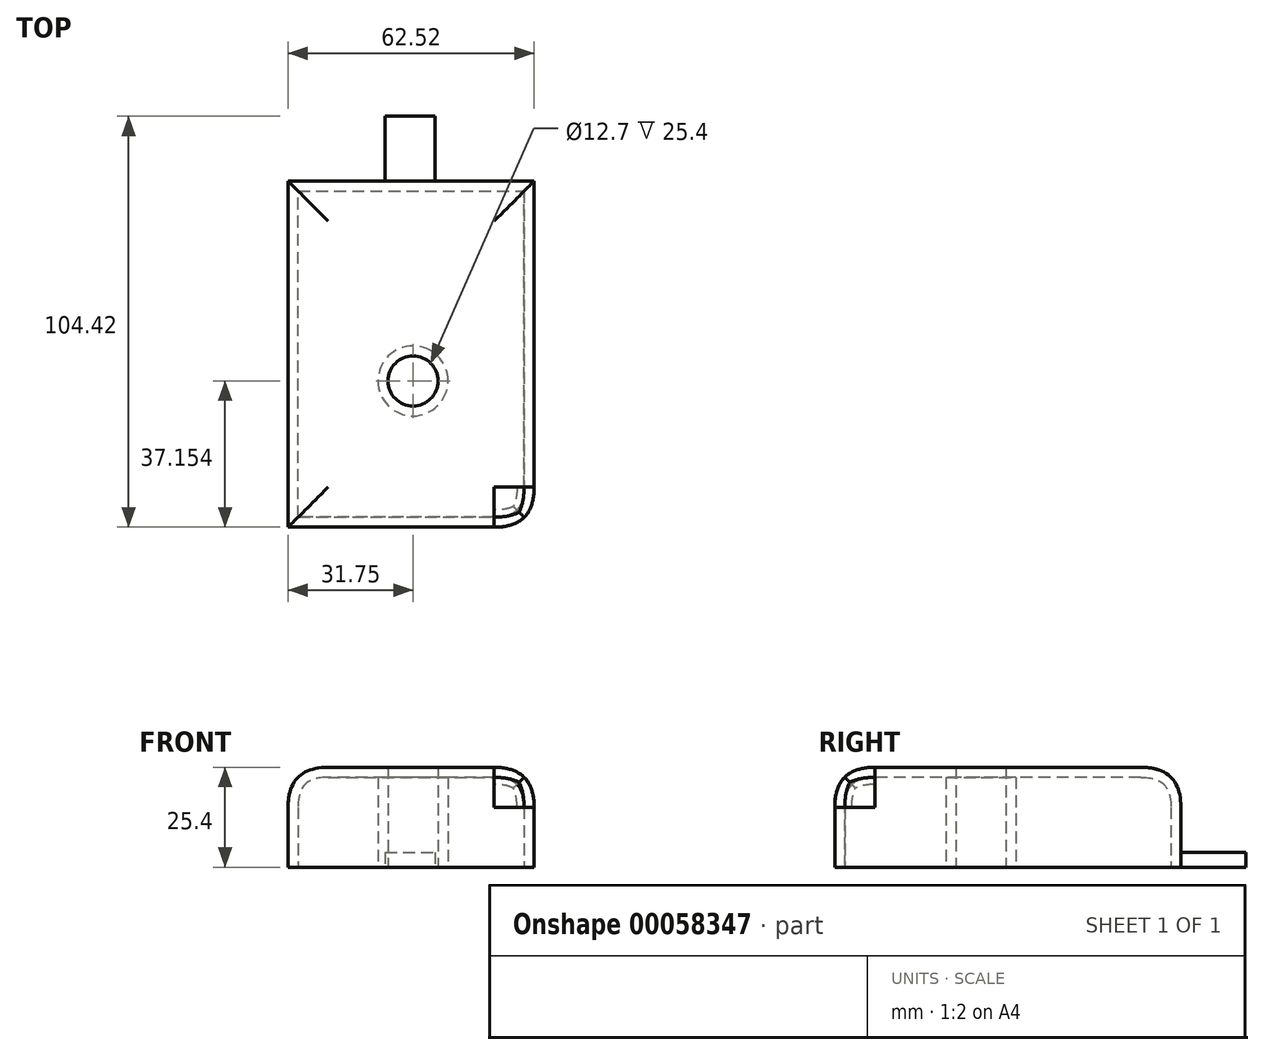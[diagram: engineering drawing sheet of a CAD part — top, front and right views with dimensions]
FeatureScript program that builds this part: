
annotation { "Feature Type Name" : "Feature", "Feature Type Description" : "" }
export const myFeature = defineFeature(function(context is Context, id is Id, definition is map)
    precondition{}
    {
        {
            var Q0;
            Q0=qCreatedBy(makeId("Top.planeOp"),FACE);
            var sketch = newSketch(context, id + "F0", { "sketchPlane" : qUnion([Q0])});
            skLineSegment(sketch, "E0.bottom", {"start": v(0, 0) * mm, "end": v(62.52, 0) * mm});
            skLineSegment(sketch, "E0.top", {"start": v(0, 87.95) * mm, "end": v(62.52, 87.95) * mm});
            skLineSegment(sketch, "E0.left", {"start": v(0, 0) * mm, "end": v(0, 87.95) * mm});
            skLineSegment(sketch, "E0.right", {"start": v(62.52, 0) * mm, "end": v(62.52, 87.95) * mm});
            skSolve(sketch);
        }
        {
            var Q0;
            Q0=makeQuery(id+"F0.imprint","IMPRINT",FACE,{"disambiguationData":[TD([[makeQuery(id+"F0.imprint","IMPRINT",EDGE,{"derivedFrom":sQuery(id+"F0.wireOp",EDGE,"E0.bottom")}),1.0]])]});
            extrude(context, id + "F1", {"entities" : qUnion([Q0]), "depth" : 25.4 * mm});
        }
        {
            var Q0;
            Q0=makeQuery(id+"F1.opExtrude","CAP_FACE",FACE,{"disambiguationData":[OSD([sQuery(id+"F0.wireOp",EDGE,"E0.bottom"),sQuery(id+"F0.wireOp",EDGE,"E0.top"),sQuery(id+"F0.wireOp",EDGE,"E0.left"),sQuery(id+"F0.wireOp",EDGE,"E0.right")])],"isStart":false});
            var sketch = newSketch(context, id + "F2", { "sketchPlane" : qUnion([Q0])});
            skPoint(sketch, "E1", {"position": v(31.75, 37.15) * mm});
            skSolve(sketch);
        }
        {
            var Q0;
            Q0=makeQuery(id+"F1.opExtrude","CAP_EDGE",EDGE,{"disambiguationData":[OSD([sQuery(id+"F0.wireOp",EDGE,"E0.right")])],"isStart":false});
            var Q1;
            Q1=makeQuery(id+"F1.opExtrude","CAP_EDGE",EDGE,{"disambiguationData":[OSD([sQuery(id+"F0.wireOp",EDGE,"E0.bottom")])],"isStart":false});
            var Q2;
            Q2=makeQuery(id+"F1.opExtrude","CAP_EDGE",EDGE,{"disambiguationData":[OSD([sQuery(id+"F0.wireOp",EDGE,"E0.left")])],"isStart":false});
            var Q3;
            Q3=makeQuery(id+"F1.opExtrude","CAP_EDGE",EDGE,{"disambiguationData":[OSD([sQuery(id+"F0.wireOp",EDGE,"E0.top")])],"isStart":false});
            var Q4;
            Q4=makeQuery(id+"F1.opExtrude","SWEPT_EDGE",EDGE,{"disambiguationData":[OSD([sQuery(id+"F0.wireOp",EDGE,"E0.bottom"),sQuery(id+"F0.wireOp",EDGE,"E0.right")])]});
            fillet(context, id + "F3", {"entities" : qUnion([Q0, Q1, Q2, Q3, Q4]), "radius" : 10.16 * mm, "tangentPropagation" : true, "rho" : 0.5, "crossSection" : FilletCrossSection.CONIC, "allowEdgeOverflow" : false});
        }
        {
            var Q0;
            Q0=sQuery(id+"F2.wireOp",VERTEX,"E1");
            var Q1;
            Q1=makeQuery(id+"F1.opExtrude","SWEPT_BODY",BODY,{"disambiguationData":[OSD([sQuery(id+"F0.wireOp",EDGE,"E0.bottom"),sQuery(id+"F0.wireOp",EDGE,"E0.top"),sQuery(id+"F0.wireOp",EDGE,"E0.left"),sQuery(id+"F0.wireOp",EDGE,"E0.right")])]});
            hole(context, id + "F4", {"style" : HoleStyle.SIMPLE, "holeDiameter" : 12.7 * mm, "endStyle" : HoleEndStyle.THROUGH, "locations" : qUnion([Q0]), "scope" : qUnion([Q1])});
        }
        {
            var Q0;
            Q0=makeQuery(id+"F1.opExtrude","CAP_FACE",FACE,{"disambiguationData":[OSD([sQuery(id+"F0.wireOp",EDGE,"E0.bottom"),sQuery(id+"F0.wireOp",EDGE,"E0.top"),sQuery(id+"F0.wireOp",EDGE,"E0.left"),sQuery(id+"F0.wireOp",EDGE,"E0.right")])],"isStart":true});
            shell(context, id + "F5", {"entities" : qUnion([Q0]), "thickness" : 2.54 * mm});
        }
        {
            var Q0;
            Q0=makeQuery(id+"F1.opExtrude","CAP_FACE",FACE,{"disambiguationData":[OSD([sQuery(id+"F0.wireOp",EDGE,"E0.bottom"),sQuery(id+"F0.wireOp",EDGE,"E0.top"),sQuery(id+"F0.wireOp",EDGE,"E0.left"),sQuery(id+"F0.wireOp",EDGE,"E0.right")])],"isStart":true});
            var sketch = newSketch(context, id + "F6", { "sketchPlane" : qUnion([Q0])});
            skLineSegment(sketch, "E2.bottom", {"start": v(24.64, -87.95) * mm, "end": v(37.34, -87.95) * mm});
            skLineSegment(sketch, "E2.top", {"start": v(24.64, -104.42) * mm, "end": v(37.34, -104.42) * mm});
            skLineSegment(sketch, "E2.left", {"start": v(24.64, -87.95) * mm, "end": v(24.64, -104.42) * mm});
            skLineSegment(sketch, "E2.right", {"start": v(37.34, -87.95) * mm, "end": v(37.34, -104.42) * mm});
            skSolve(sketch);
        }
        {
            var Q0;
            Q0=makeQuery(id+"F6.imprint","IMPRINT",FACE,{"disambiguationData":[TD([[makeQuery(id+"F6.imprint","IMPRINT",EDGE,{"derivedFrom":sQuery(id+"F6.wireOp",EDGE,"E2.bottom")}),-1.0]])]});
            extrude(context, id + "F7", {"entities" : qUnion([Q0]), "oppositeDirection" : true, "depth" : 3.8 * mm});
        }
    });
